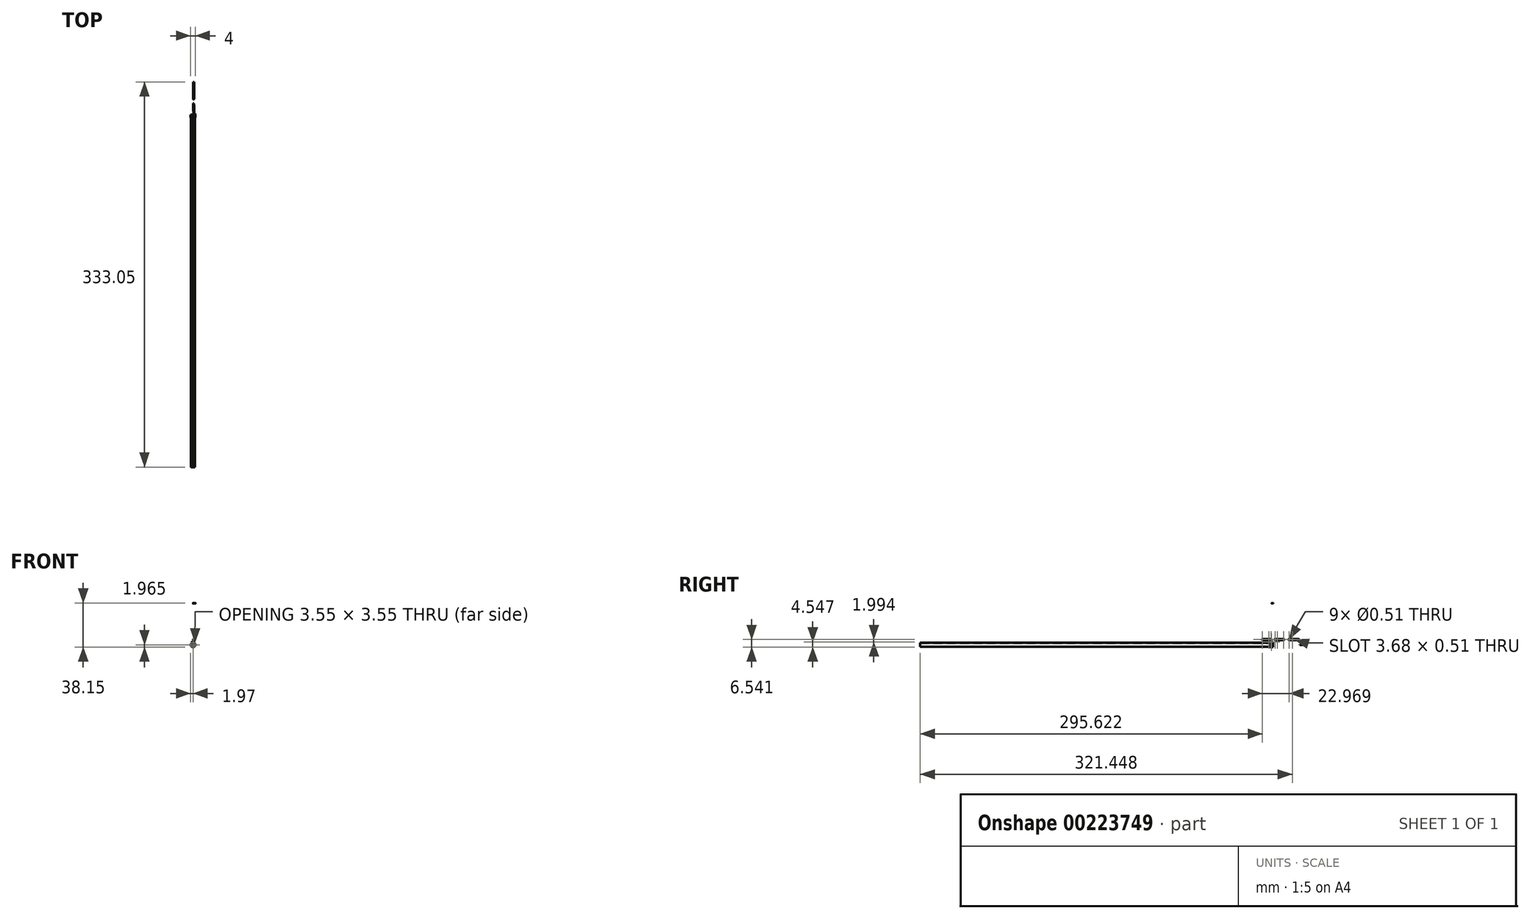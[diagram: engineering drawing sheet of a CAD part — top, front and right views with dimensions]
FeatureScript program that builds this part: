
annotation { "Feature Type Name" : "Feature", "Feature Type Description" : "" }
export const myFeature = defineFeature(function(context is Context, id is Id, definition is map)
    precondition{}
    {
        {
            var Q0;
            Q0=qCreatedBy(makeId("Right.planeOp"),FACE);
            var sketch = newSketch(context, id + "F0", { "sketchPlane" : qUnion([Q0])});
            skLineSegment(sketch, "E0.bottom", {"start": v(-9.69, 5.08) * mm, "end": v(-1.17, 5.08) * mm});
            skLineSegment(sketch, "E0.top", {"start": v(-9.69, 4.06) * mm, "end": v(-1.17, 4.06) * mm});
            skLineSegment(sketch, "E0.left", {"start": v(-9.69, 5.08) * mm, "end": v(-9.69, 4.06) * mm});
            skLineSegment(sketch, "E0.right", {"start": v(-1.17, 5.08) * mm, "end": v(-1.17, 4.06) * mm});
            skCircle(sketch, "E1", {"center": v(-9.18, 4.57) * mm, "radius": 0.25 * mm});
            skCircle(sketch, "E2", {"center": v(-1.68, 4.57) * mm, "radius": 0.25 * mm});
            skCircle(sketch, "E3", {"center": v(-3.71, 4.57) * mm, "radius": 0.25 * mm});
            skLineSegment(sketch, "E4", {"start": v(-9.69, 4.57) * mm, "end": v(-1.17, 4.57) * mm, "construction": true});
            skLineSegment(sketch, "E5.MirrorCS", {"start": v(-9.69, 4.06) * mm, "end": v(-9.69, 5.08) * mm});
            skLineSegment(sketch, "E6.MirrorCS", {"start": v(-1.17, 4.06) * mm, "end": v(-1.17, 5.08) * mm});
            skLineSegment(sketch, "E7", {"start": v(0, 0) * mm, "end": v(0, 11.35) * mm, "construction": true});
            skLineSegment(sketch, "E8.MirrorCS", {"start": v(9.69, 5.08) * mm, "end": v(9.69, 4.06) * mm});
            skLineSegment(sketch, "E9.MirrorCS", {"start": v(1.17, 4.06) * mm, "end": v(1.17, 5.08) * mm});
            skCircle(sketch, "E10.MirrorC", {"center": v(1.68, 4.57) * mm, "radius": 0.25 * mm});
            skCircle(sketch, "E11.MirrorC", {"center": v(3.71, 4.57) * mm, "radius": 0.25 * mm});
            skLineSegment(sketch, "E12.MirrorCS", {"start": v(9.69, 5.08) * mm, "end": v(1.17, 5.08) * mm});
            skLineSegment(sketch, "E13.MirrorCS", {"start": v(9.69, 4.06) * mm, "end": v(1.17, 4.06) * mm});
            skCircle(sketch, "E14.MirrorC", {"center": v(9.18, 4.57) * mm, "radius": 0.25 * mm});
            skLineSegment(sketch, "E15.MirrorCS", {"start": v(1.17, 5.08) * mm, "end": v(1.17, 4.06) * mm});
            skLineSegment(sketch, "E16.MirrorCS", {"start": v(9.69, 4.06) * mm, "end": v(9.69, 5.08) * mm});
            skLineSegment(sketch, "E17.MirrorCS", {"start": v(9.69, 4.57) * mm, "end": v(1.17, 4.57) * mm, "construction": true});
            skLineSegment(sketch, "E18.bottom", {"start": v(13.28, 5.08) * mm, "end": v(22.68, 5.08) * mm});
            skLineSegment(sketch, "E18.top", {"start": v(13.28, 4.06) * mm, "end": v(22.68, 4.06) * mm});
            skLineSegment(sketch, "E18.left", {"start": v(13.28, 5.08) * mm, "end": v(13.28, 4.06) * mm});
            skLineSegment(sketch, "E18.right", {"start": v(22.68, 5.08) * mm, "end": v(22.68, 4.06) * mm});
            skLineSegment(sketch, "E19", {"start": v(13.28, 4.57) * mm, "end": v(22.68, 4.57) * mm, "construction": true});
            skCircle(sketch, "E20", {"center": v(13.8, 4.57) * mm, "radius": 0.25 * mm});
            skLineSegment(sketch, "E21.bottom", {"start": v(15.06, 4.82) * mm, "end": v(18.24, 4.82) * mm});
            skLineSegment(sketch, "E21.top", {"start": v(15.06, 4.32) * mm, "end": v(18.24, 4.32) * mm});
            skLineSegment(sketch, "E21.left", {"start": v(14.8, 4.57) * mm, "end": v(14.8, 4.57) * mm});
            skLineSegment(sketch, "E21.right", {"start": v(18.49, 4.57) * mm, "end": v(18.49, 4.57) * mm});
            skPoint(sketch, "E22", {"position": v(14.8, 4.57) * mm});
            skPoint(sketch, "E23.visualSharp", {"position": v(18.49, 4.82) * mm});
            skArc(sketch, "E23.filletArc", {"start": v(18.49, 4.57) * mm, "mid": v(18.41, 4.75) * mm, "end": v(18.24, 4.82) * mm});
            skPoint(sketch, "E24.visualSharp", {"position": v(18.49, 4.32) * mm});
            skArc(sketch, "E24.filletArc", {"start": v(18.24, 4.32) * mm, "mid": v(18.41, 4.4) * mm, "end": v(18.49, 4.57) * mm});
            skPoint(sketch, "E25.visualSharp", {"position": v(14.8, 4.82) * mm});
            skArc(sketch, "E25.filletArc", {"start": v(15.06, 4.82) * mm, "mid": v(14.88, 4.75) * mm, "end": v(14.8, 4.57) * mm});
            skPoint(sketch, "E26.visualSharp", {"position": v(14.8, 4.32) * mm});
            skArc(sketch, "E26.filletArc", {"start": v(14.8, 4.57) * mm, "mid": v(14.88, 4.4) * mm, "end": v(15.06, 4.32) * mm});
            skSolve(sketch);
        }
        {
            var Q0;
            Q0=qSketchRegion(id+"F0",true);
            extrude(context, id + "F1", {"entities" : qUnion([Q0]), "depth" : 1.02 * mm});
        }
        {
            var Q0;
            Q0=makeQuery(id+"F1.opExtrude","SWEPT_FACE",FACE,{"disambiguationData":[OSD([sQuery(id+"F0.wireOp",EDGE,"E0.bottom")])]});
            var sketch = newSketch(context, id + "F2", { "sketchPlane" : qUnion([Q0])});
            skLineSegment(sketch, "E27.0", {"start": v(1.02, 22.68) * mm, "end": v(0, 22.68) * mm, "construction": true});
            skLineSegment(sketch, "E28", {"start": v(0.5, -9.69) * mm, "end": v(0.5, 22.68) * mm, "construction": true});
            skLineSegment(sketch, "E29.bottom", {"start": v(0, -8.42) * mm, "end": v(0.25, -8.42) * mm});
            skLineSegment(sketch, "E29.top", {"start": v(0, -9.69) * mm, "end": v(0.25, -9.69) * mm});
            skLineSegment(sketch, "E29.left", {"start": v(0, -8.42) * mm, "end": v(0, -9.69) * mm});
            skLineSegment(sketch, "E29.right", {"start": v(0.25, -8.42) * mm, "end": v(0.25, -9.69) * mm});
            skLineSegment(sketch, "E30.MirrorCS", {"start": v(1.02, -8.42) * mm, "end": v(0.76, -8.42) * mm});
            skLineSegment(sketch, "E31.MirrorCS", {"start": v(1.02, -9.69) * mm, "end": v(0.76, -9.69) * mm});
            skLineSegment(sketch, "E32.MirrorCS", {"start": v(0.76, -8.42) * mm, "end": v(0.76, -9.69) * mm});
            skLineSegment(sketch, "E33.MirrorCS", {"start": v(1.02, -8.42) * mm, "end": v(1.02, -9.69) * mm});
            skLineSegment(sketch, "E34.bottom", {"start": v(0.5, -1.17) * mm, "end": v(1.02, -1.17) * mm});
            skLineSegment(sketch, "E34.top", {"start": v(0.5, -2.95) * mm, "end": v(1.02, -2.95) * mm});
            skLineSegment(sketch, "E34.left", {"start": v(0.5, -1.17) * mm, "end": v(0.5, -2.95) * mm});
            skLineSegment(sketch, "E34.right", {"start": v(1.02, -1.17) * mm, "end": v(1.02, -2.95) * mm});
            skLineSegment(sketch, "E35.bottom", {"start": v(0.5, 1.17) * mm, "end": v(0, 1.17) * mm});
            skLineSegment(sketch, "E35.top", {"start": v(0.5, 2.95) * mm, "end": v(0, 2.95) * mm});
            skLineSegment(sketch, "E35.left", {"start": v(0.5, 1.17) * mm, "end": v(0.5, 2.95) * mm});
            skLineSegment(sketch, "E35.right", {"start": v(0, 1.17) * mm, "end": v(0, 2.95) * mm});
            skLineSegment(sketch, "E36.bottom", {"start": v(0, 9.69) * mm, "end": v(0.25, 9.69) * mm});
            skLineSegment(sketch, "E36.top", {"start": v(0, 8.42) * mm, "end": v(0.25, 8.42) * mm});
            skLineSegment(sketch, "E36.left", {"start": v(0, 9.69) * mm, "end": v(0, 8.42) * mm});
            skLineSegment(sketch, "E36.right", {"start": v(0.25, 9.69) * mm, "end": v(0.25, 8.42) * mm});
            skLineSegment(sketch, "E37.MirrorCS", {"start": v(1.02, 9.69) * mm, "end": v(0.76, 9.69) * mm});
            skLineSegment(sketch, "E38.MirrorCS", {"start": v(1.02, 9.69) * mm, "end": v(1.02, 8.42) * mm});
            skLineSegment(sketch, "E39.MirrorCS", {"start": v(1.02, 8.42) * mm, "end": v(0.76, 8.42) * mm});
            skLineSegment(sketch, "E40.MirrorCS", {"start": v(0.76, 9.69) * mm, "end": v(0.76, 8.42) * mm});
            skSolve(sketch);
        }
        {
            var Q0;
            Q0 = qSketchRegion(id + "F2", true);
            extrude(context, id + "F3", {"entities" : qUnion([Q0]), "operationType" : NewBodyOperationType.REMOVE, "endBound" : BoundingType.THROUGH_ALL, "oppositeDirection" : true, "depth" : 25.4 * mm});
        }
        {
            var Q0;
            Q0=makeQuery(id+"F1.opExtrude","SWEPT_EDGE",EDGE,{"disambiguationData":[OSD([sQuery(id+"F0.wireOp",EDGE,"E0.bottom"),sQuery(id+"F0.wireOp",EDGE,"E0.left")])]});
            var Q1;
            Q1=makeQuery(id+"F1.opExtrude","SWEPT_EDGE",EDGE,{"disambiguationData":[OSD([sQuery(id+"F0.wireOp",EDGE,"E0.top"),sQuery(id+"F0.wireOp",EDGE,"E0.left")])]});
            var Q2;
            Q2=makeQuery(id+"F1.opExtrude","SWEPT_EDGE",EDGE,{"disambiguationData":[OSD([sQuery(id+"F0.wireOp",EDGE,"E0.bottom"),sQuery(id+"F0.wireOp",EDGE,"E0.right")])]});
            var Q3;
            Q3=makeQuery(id+"F1.opExtrude","SWEPT_EDGE",EDGE,{"disambiguationData":[OSD([sQuery(id+"F0.wireOp",EDGE,"E0.top"),sQuery(id+"F0.wireOp",EDGE,"E0.right")])]});
            var Q4;
            Q4=makeQuery(id+"F1.opExtrude","SWEPT_EDGE",EDGE,{"disambiguationData":[OSD([sQuery(id+"F0.wireOp",EDGE,"E12.MirrorCS"),sQuery(id+"F0.wireOp",EDGE,"E15.MirrorCS")])]});
            var Q5;
            Q5=makeQuery(id+"F1.opExtrude","SWEPT_EDGE",EDGE,{"disambiguationData":[OSD([sQuery(id+"F0.wireOp",EDGE,"E15.MirrorCS"),sQuery(id+"F0.wireOp",EDGE,"E13.MirrorCS")])]});
            var Q6;
            Q6=makeQuery(id+"F1.opExtrude","SWEPT_EDGE",EDGE,{"disambiguationData":[OSD([sQuery(id+"F0.wireOp",EDGE,"E16.MirrorCS"),sQuery(id+"F0.wireOp",EDGE,"E12.MirrorCS")])]});
            var Q7;
            Q7=makeQuery(id+"F1.opExtrude","SWEPT_EDGE",EDGE,{"disambiguationData":[OSD([sQuery(id+"F0.wireOp",EDGE,"E16.MirrorCS"),sQuery(id+"F0.wireOp",EDGE,"E13.MirrorCS")])]});
            var Q8;
            Q8=makeQuery(id+"F1.opExtrude","SWEPT_EDGE",EDGE,{"disambiguationData":[OSD([sQuery(id+"F0.wireOp",EDGE,"E18.bottom"),sQuery(id+"F0.wireOp",EDGE,"E18.left")])]});
            var Q9;
            Q9=makeQuery(id+"F1.opExtrude","SWEPT_EDGE",EDGE,{"disambiguationData":[OSD([sQuery(id+"F0.wireOp",EDGE,"E18.top"),sQuery(id+"F0.wireOp",EDGE,"E18.left")])]});
            var Q10;
            Q10=makeQuery(id+"F1.opExtrude","SWEPT_EDGE",EDGE,{"disambiguationData":[OSD([sQuery(id+"F0.wireOp",EDGE,"E18.bottom"),sQuery(id+"F0.wireOp",EDGE,"E18.right")])]});
            var Q11;
            Q11=makeQuery(id+"F1.opExtrude","SWEPT_EDGE",EDGE,{"disambiguationData":[OSD([sQuery(id+"F0.wireOp",EDGE,"E18.top"),sQuery(id+"F0.wireOp",EDGE,"E18.right")])]});
            fillet(context, id + "F4", {"entities" : qUnion([Q0, Q1, Q2, Q3, Q4, Q5, Q6, Q7, Q8, Q9, Q10, Q11]), "radius" : 0.5 * mm, "tangentPropagation" : true, "allowEdgeOverflow" : false});
        }
        {
            var Q0;
            Q0=makeQuery(id+"F3.boolean.opBoolean","COPY",EDGE,{"derivedFrom":makeQuery(id+"F3.opExtrude","CAP_EDGE",EDGE,{"disambiguationData":[OSD([sQuery(id+"F2.wireOp",EDGE,"E34.top")])],"isStart":true})});
            var Q1;
            Q1=makeQuery(id+"F3.boolean.opBoolean","INTERSECT",EDGE,{"derivedFrom":[makeQuery(id+"F1.opExtrude","SWEPT_FACE",FACE,{"disambiguationData":[OSD([sQuery(id+"F0.wireOp",EDGE,"E0.top")])]}),makeQuery(id+"F3.opExtrude","SWEPT_FACE",FACE,{"disambiguationData":[OSD([sQuery(id+"F2.wireOp",EDGE,"E34.top")])]})]});
            var Q2;
            Q2=makeQuery(id+"F3.boolean.opBoolean","INTERSECT",EDGE,{"derivedFrom":[makeQuery(id+"F1.opExtrude","SWEPT_FACE",FACE,{"disambiguationData":[OSD([sQuery(id+"F0.wireOp",EDGE,"E0.top")])]}),makeQuery(id+"F3.opExtrude","SWEPT_FACE",FACE,{"disambiguationData":[OSD([sQuery(id+"F2.wireOp",EDGE,"E29.bottom")])]})]});
            var Q3;
            Q3=makeQuery(id+"F3.boolean.opBoolean","COPY",EDGE,{"derivedFrom":makeQuery(id+"F3.opExtrude","CAP_EDGE",EDGE,{"disambiguationData":[OSD([sQuery(id+"F2.wireOp",EDGE,"E29.bottom")])],"isStart":true})});
            var Q4;
            Q4=makeQuery(id+"F3.boolean.opBoolean","COPY",EDGE,{"derivedFrom":makeQuery(id+"F3.opExtrude","CAP_EDGE",EDGE,{"disambiguationData":[OSD([sQuery(id+"F2.wireOp",EDGE,"E30.MirrorCS")])],"isStart":true})});
            var Q5;
            Q5=makeQuery(id+"F3.boolean.opBoolean","INTERSECT",EDGE,{"derivedFrom":[makeQuery(id+"F1.opExtrude","SWEPT_FACE",FACE,{"disambiguationData":[OSD([sQuery(id+"F0.wireOp",EDGE,"E0.top")])]}),makeQuery(id+"F3.opExtrude","SWEPT_FACE",FACE,{"disambiguationData":[OSD([sQuery(id+"F2.wireOp",EDGE,"E30.MirrorCS")])]})]});
            var Q6;
            Q6=makeQuery(id+"F3.boolean.opBoolean","COPY",EDGE,{"derivedFrom":makeQuery(id+"F3.opExtrude","CAP_EDGE",EDGE,{"disambiguationData":[OSD([sQuery(id+"F2.wireOp",EDGE,"E35.top")])],"isStart":true})});
            var Q7;
            Q7=makeQuery(id+"F3.boolean.opBoolean","INTERSECT",EDGE,{"derivedFrom":[makeQuery(id+"F1.opExtrude","SWEPT_FACE",FACE,{"disambiguationData":[OSD([sQuery(id+"F0.wireOp",EDGE,"E13.MirrorCS")])]}),makeQuery(id+"F3.opExtrude","SWEPT_FACE",FACE,{"disambiguationData":[OSD([sQuery(id+"F2.wireOp",EDGE,"E35.top")])]})]});
            var Q8;
            Q8=makeQuery(id+"F3.boolean.opBoolean","COPY",EDGE,{"derivedFrom":makeQuery(id+"F3.opExtrude","CAP_EDGE",EDGE,{"disambiguationData":[OSD([sQuery(id+"F2.wireOp",EDGE,"E36.top")])],"isStart":true})});
            var Q9;
            Q9=makeQuery(id+"F3.boolean.opBoolean","INTERSECT",EDGE,{"derivedFrom":[makeQuery(id+"F1.opExtrude","SWEPT_FACE",FACE,{"disambiguationData":[OSD([sQuery(id+"F0.wireOp",EDGE,"E13.MirrorCS")])]}),makeQuery(id+"F3.opExtrude","SWEPT_FACE",FACE,{"disambiguationData":[OSD([sQuery(id+"F2.wireOp",EDGE,"E36.top")])]})]});
            var Q10;
            Q10=makeQuery(id+"F3.boolean.opBoolean","COPY",EDGE,{"derivedFrom":makeQuery(id+"F3.opExtrude","CAP_EDGE",EDGE,{"disambiguationData":[OSD([sQuery(id+"F2.wireOp",EDGE,"E39.MirrorCS")])],"isStart":true})});
            var Q11;
            Q11=makeQuery(id+"F3.boolean.opBoolean","INTERSECT",EDGE,{"derivedFrom":[makeQuery(id+"F1.opExtrude","SWEPT_FACE",FACE,{"disambiguationData":[OSD([sQuery(id+"F0.wireOp",EDGE,"E13.MirrorCS")])]}),makeQuery(id+"F3.opExtrude","SWEPT_FACE",FACE,{"disambiguationData":[OSD([sQuery(id+"F2.wireOp",EDGE,"E39.MirrorCS")])]})]});
            fillet(context, id + "F5", {"entities" : qUnion([Q0, Q1, Q2, Q3, Q4, Q5, Q6, Q7, Q8, Q9, Q10, Q11]), "radius" : 0.13 * mm, "tangentPropagation" : true, "allowEdgeOverflow" : false});
        }
        {
            var Q0;
            Q0=qCreatedBy(makeId("Front.planeOp"),FACE);
            var sketch = newSketch(context, id + "F6", { "sketchPlane" : qUnion([Q0])});
            skArc(sketch, "E41", {"start": v(-0.25, 1.7) * mm, "mid": v(0, -1.71) * mm, "end": v(0.25, 1.7) * mm});
            skArc(sketch, "E42", {"start": v(-0.25, 1.24) * mm, "mid": v(0, -1.27) * mm, "end": v(0.25, 1.24) * mm});
            skLineSegment(sketch, "E43", {"start": v(-0.25, 1.7) * mm, "end": v(-0.25, 1.24) * mm});
            skLineSegment(sketch, "E44", {"start": v(0, 0) * mm, "end": v(0, 2.64) * mm, "construction": true});
            skLineSegment(sketch, "E45.MirrorCS", {"start": v(0.25, 1.7) * mm, "end": v(0.25, 1.24) * mm});
            skSolve(sketch);
        }
        {
            var Q0;
            Q0=qSketchRegion(id+"F6",true);
            extrude(context, id + "F7", {"entities" : qUnion([Q0]), "depth" : 304.8 * mm});
        }
        {
            var Q0;
            Q0=qCreatedBy(makeId("Front.planeOp"),FACE);
            var sketch = newSketch(context, id + "F8", { "sketchPlane" : qUnion([Q0])});
            skArc(sketch, "E46", {"start": v(-0.2, 1.77) * mm, "mid": v(0, -1.78) * mm, "end": v(0.2, 1.77) * mm});
            skArc(sketch, "E47", {"start": v(-0.76, 1.82) * mm, "mid": v(0, -1.97) * mm, "end": v(0.76, 1.82) * mm});
            skLineSegment(sketch, "E48", {"start": v(0, 0) * mm, "end": v(0, 3.84) * mm, "construction": true});
            skLineSegment(sketch, "E49", {"start": v(-0.76, 1.82) * mm, "end": v(-0.76, 3.34) * mm});
            skLineSegment(sketch, "E50", {"start": v(-0.76, 3.34) * mm, "end": v(0, 3.34) * mm});
            skLineSegment(sketch, "E51.MirrorCS", {"start": v(0.76, 1.82) * mm, "end": v(0.76, 3.34) * mm});
            skLineSegment(sketch, "E52.MirrorCS", {"start": v(0.76, 3.34) * mm, "end": v(0, 3.34) * mm});
            skLineSegment(sketch, "E53", {"start": v(-0.2, 1.77) * mm, "end": v(-0.2, 1.27) * mm});
            skLineSegment(sketch, "E54", {"start": v(-0.2, 1.27) * mm, "end": v(0.2, 1.27) * mm});
            skLineSegment(sketch, "E55", {"start": v(0.2, 1.27) * mm, "end": v(0.2, 1.77) * mm});
            skSolve(sketch);
        }
        {
            var Q0;
            Q0=qSketchRegion(id+"F8",true);
            extrude(context, id + "F9", {"entities" : qUnion([Q0]), "depth" : 2.54 * mm});
        }
        {
            var Q0;
            Q0=qCreatedBy(makeId("Front.planeOp"),FACE);
            var sketch = newSketch(context, id + "F10", { "sketchPlane" : qUnion([Q0])});
            skLineSegment(sketch, "E56", {"start": v(0, 1.46) * mm, "end": v(0, 3.38) * mm, "construction": true});
            skLineSegment(sketch, "E57.bottom", {"start": v(-0.25, 1.97) * mm, "end": v(0.25, 1.97) * mm});
            skLineSegment(sketch, "E57.top", {"start": v(-0.25, 3.5) * mm, "end": v(0.25, 3.5) * mm});
            skLineSegment(sketch, "E57.left", {"start": v(-0.25, 1.97) * mm, "end": v(-0.25, 3.5) * mm});
            skLineSegment(sketch, "E57.right", {"start": v(0.25, 1.97) * mm, "end": v(0.25, 3.5) * mm});
            skCircle(sketch, "E58", {"center": v(0, 0) * mm, "radius": 1.97 * mm, "construction": true});
            skSolve(sketch);
        }
        {
            var Q0;
            Q0=makeQuery(id+"F10.imprint","IMPRINT",FACE,{"disambiguationData":[TD([[makeQuery(id+"F10.imprint","IMPRINT",EDGE,{"derivedFrom":sQuery(id+"F10.wireOp",EDGE,"E57.bottom")}),1.0]])]});
            extrude(context, id + "F11", {"entities" : qUnion([Q0]), "operationType" : NewBodyOperationType.REMOVE, "endBound" : BoundingType.THROUGH_ALL, "depth" : 25.4 * mm});
        }
        {
            var Q0;
            Q0=qCreatedBy(makeId("Right.planeOp"),FACE);
            var sketch = newSketch(context, id + "F12", { "sketchPlane" : qUnion([Q0])});
            skCircle(sketch, "E59", {"center": v(-1.27, 2.58) * mm, "radius": 0.25 * mm});
            skLineSegment(sketch, "E60", {"start": v(0, 3.34) * mm, "end": v(0, 1.97) * mm});
            skLineSegment(sketch, "E61", {"start": v(-1.78, 1.97) * mm, "end": v(-1.78, 2.58) * mm});
            skLineSegment(sketch, "E62", {"start": v(-1.27, 2.92) * mm, "end": v(-1.27, 1.82) * mm, "construction": true});
            skLineSegment(sketch, "E63", {"start": v(-0.76, 1.97) * mm, "end": v(-0.76, 2.58) * mm});
            skArc(sketch, "E64", {"start": v(-0.76, 2.58) * mm, "mid": v(-1.27, 3.09) * mm, "end": v(-1.78, 2.58) * mm});
            skLineSegment(sketch, "E65", {"start": v(-2.54, 3.34) * mm, "end": v(-2.2, 3.54) * mm});
            skLineSegment(sketch, "E66", {"start": v(-2.2, 3.54) * mm, "end": v(-0.65, 3.54) * mm});
            skLineSegment(sketch, "E67", {"start": v(-0.65, 3.54) * mm, "end": v(0, 3.34) * mm});
            skLineSegment(sketch, "E68", {"start": v(-2.54, 3.34) * mm, "end": v(-2.54, 1.97) * mm});
            skLineSegment(sketch, "E69", {"start": v(-2.54, 1.97) * mm, "end": v(-1.78, 1.97) * mm});
            skLineSegment(sketch, "E70", {"start": v(-0.76, 1.97) * mm, "end": v(0, 1.97) * mm});
            skLineSegment(sketch, "E71.0", {"start": v(-2.54, 3.34) * mm, "end": v(0, 3.34) * mm, "construction": true});
            skPoint(sketch, "E72", {"position": v(-1.27, 3.34) * mm});
            skSolve(sketch);
        }
        {
            var Q0;
            Q0=qSketchRegion(id+"F12",true);
            extrude(context, id + "F13", {"entities" : qUnion([Q0]), "operationType" : NewBodyOperationType.REMOVE, "endBound" : BoundingType.THROUGH_ALL, "oppositeDirection" : true, "depth" : 25.4 * mm, "hasSecondDirection" : true, "secondDirectionBound" : SecondDirectionBoundingType.THROUGH_ALL, "secondDirectionOppositeDirection" : false, "secondDirectionDepth" : 25.4 * mm});
        }
        {
            var Q0;
            Q0=makeQuery(id+"F9.opExtrude","SWEPT_EDGE",EDGE,{"disambiguationData":[OSD([sQuery(id+"F8.wireOp",EDGE,"E47"),sQuery(id+"F8.wireOp",EDGE,"E51.MirrorCS")])]});
            var Q1;
            Q1=makeQuery(id+"F9.opExtrude","SWEPT_EDGE",EDGE,{"disambiguationData":[OSD([sQuery(id+"F8.wireOp",EDGE,"E47"),sQuery(id+"F8.wireOp",EDGE,"E49")])]});
            fillet(context, id + "F14", {"entities" : qUnion([Q0, Q1]), "radius" : 0.25 * mm, "tangentPropagation" : true, "allowEdgeOverflow" : false});
        }
        {
            var Q0;
            Q0=qCreatedBy(makeId("Right.planeOp"),FACE);
            var sketch = newSketch(context, id + "F15", { "sketchPlane" : qUnion([Q0])});
            skCircle(sketch, "E73", {"center": v(0, 35.94) * mm, "radius": 0.23 * mm});
            skSolve(sketch);
        }
        {
            var Q0;
            Q0=qSketchRegion(id+"F15",true);
            extrude(context, id + "F16", {"entities" : qUnion([Q0]), "depth" : 2.03 * mm});
        }
        {
            var Q0;
            Q0=qCreatedBy(makeId("Right.planeOp"),FACE);
            var sketch = newSketch(context, id + "F17", { "sketchPlane" : qUnion([Q0])});
            skCircle(sketch, "E74", {"center": v(-1.04, 35.95) * mm, "radius": 0.23 * mm});
            skSolve(sketch);
        }
        {
            var Q0;
            Q0 = qSketchRegion(id + "F17", true);
            var Q1;
            Q1=sQuery(id+"F17.wireOp",EDGE,"E74");
            extrude(context, id + "F18", {"entities" : qUnion([Q0]), "surfaceEntities" : qUnion([Q1]), "depth" : 1.02 * mm});
        }
        {
            var Q0;
            Q0=qCreatedBy(makeId("Top.planeOp"),FACE);
            var sketch = newSketch(context, id + "F19", { "sketchPlane" : qUnion([Q0])});
            skLineSegment(sketch, "E75.bottom", {"start": v(0, 28.25) * mm, "end": v(1.02, 28.25) * mm});
            skLineSegment(sketch, "E75.top", {"start": v(0, 23.17) * mm, "end": v(1.02, 23.17) * mm});
            skLineSegment(sketch, "E75.left", {"start": v(0, 28.25) * mm, "end": v(0, 23.17) * mm});
            skLineSegment(sketch, "E75.right", {"start": v(1.02, 28.25) * mm, "end": v(1.02, 23.17) * mm});
            skSolve(sketch);
        }
        {
            var Q0;
            Q0=makeQuery(id+"F19.imprint","IMPRINT",FACE,{"disambiguationData":[TD([[makeQuery(id+"F19.imprint","IMPRINT",EDGE,{"derivedFrom":sQuery(id+"F19.wireOp",EDGE,"E75.bottom")}),-1.0]])]});
            extrude(context, id + "F20", {"entities" : qUnion([Q0]), "depth" : .1 * mm});
        }
    });
